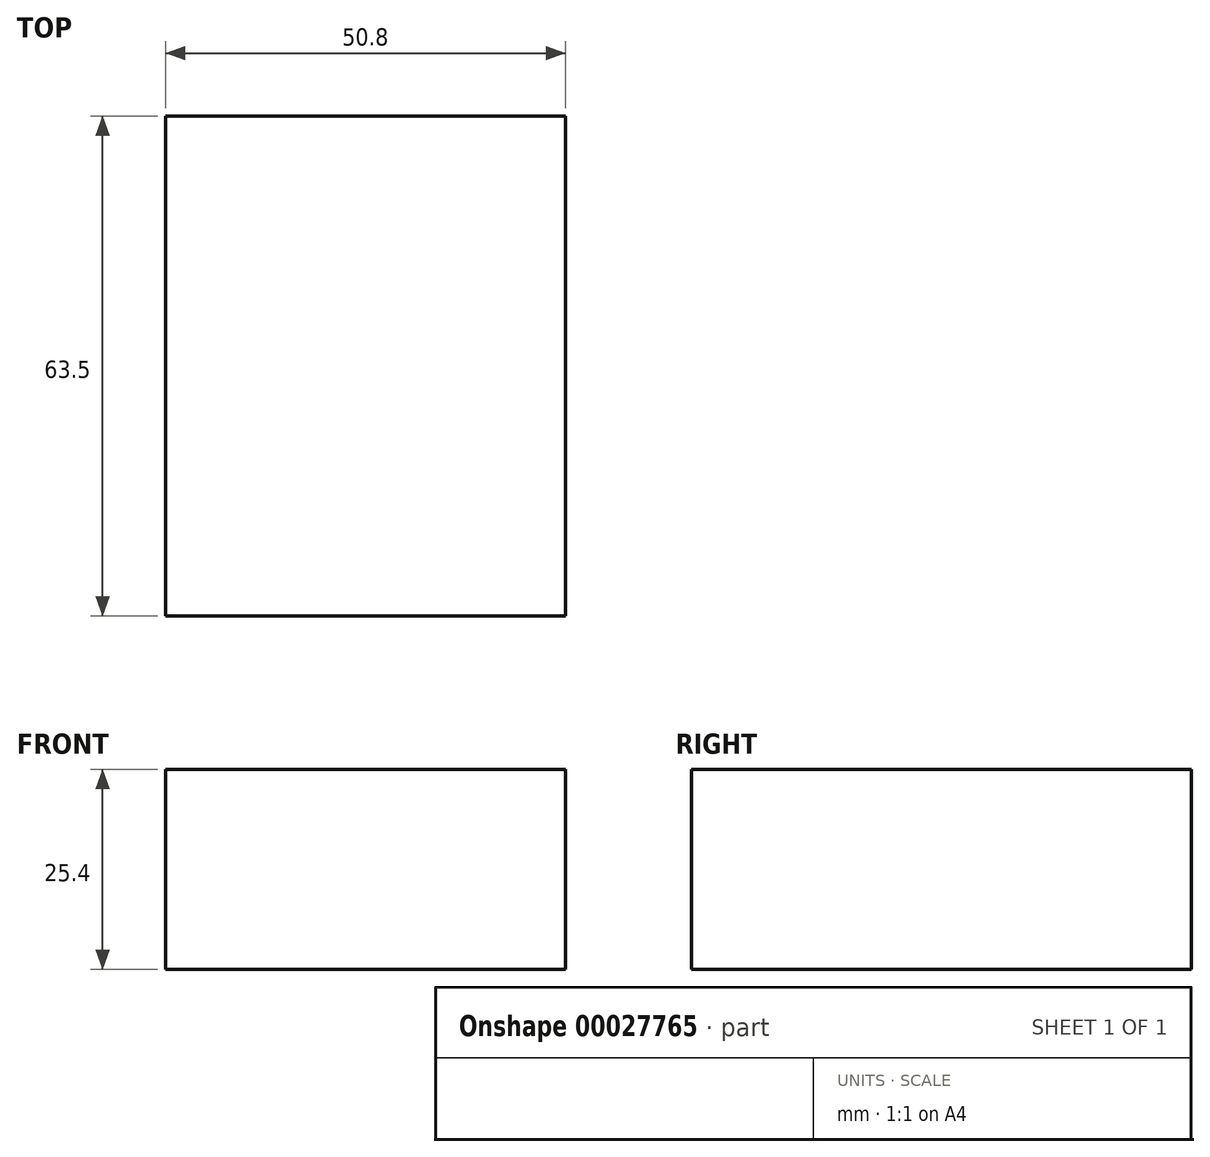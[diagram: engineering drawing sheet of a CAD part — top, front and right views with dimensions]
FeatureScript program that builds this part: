
annotation { "Feature Type Name" : "Feature", "Feature Type Description" : "" }
export const myFeature = defineFeature(function(context is Context, id is Id, definition is map)
    precondition{}
    {
        {
            var Q0;
            Q0=qCreatedBy(makeId("Top.planeOp"),FACE);
            var sketch = newSketch(context, id + "F0", { "sketchPlane" : qUnion([Q0])});
            skLineSegment(sketch, "E0.bottom", {"start": v(0, 0) * mm, "end": v(50.8, 0) * mm});
            skLineSegment(sketch, "E0.top", {"start": v(0, 63.5) * mm, "end": v(50.8, 63.5) * mm});
            skLineSegment(sketch, "E0.left", {"start": v(0, 0) * mm, "end": v(0, 63.5) * mm});
            skLineSegment(sketch, "E0.right", {"start": v(50.8, 0) * mm, "end": v(50.8, 63.5) * mm});
            skSolve(sketch);
        }
        {
            var Q0;
            Q0=makeQuery(id+"F0.imprint","IMPRINT",FACE,{"disambiguationData":[TD([[makeQuery(id+"F0.imprint","IMPRINT",EDGE,{"derivedFrom":sQuery(id+"F0.wireOp",EDGE,"E0.bottom")}),1.0]])]});
            extrude(context, id + "F1", {"entities" : qUnion([Q0]), "depth" : 25.4 * mm});
        }
    });
